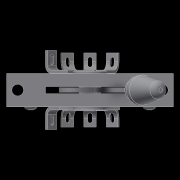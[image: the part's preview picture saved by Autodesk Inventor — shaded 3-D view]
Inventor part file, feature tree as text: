
AUTODESK INVENTOR PART (.ipt)
format: ipt  version: 2020 (Build 240168000, 168)  size: 740,352 bytes
history: native  units: in
note: dims shown in document units (in); Inventor stores cm internally (conversion verified against a paired STEP export)
features: other x22, extrude x20, projected_geometry x5, fillet x3, mirror x1, sketch x1
ambient origin geometry x8: Origin, YZ Plane, XZ Plane, XY Plane, X Axis, Y Axis, Z Axis, Center Point
bodies: Solid3 (feature_tree), Solid5 (feature_tree), Solid6 (feature_tree), Solid7 (feature_tree), Solid8 (feature_tree)
feature tree (52):
  other  "TopProfile"
  extrude  "FrontPanelFeature"  Depth=0.1in
  extrude  "SideFeature"  Depth=0.1in
  other  "SideProfile"
  extrude  "SideProfileFeature"  Depth=0.1in
  extrude  "SideMountsFeature"  Depth=0.1in
  extrude  "MiddleExtrusionFeature"  Depth=0.1in
  extrude  "SideIndentsFeature"  Depth=0.1in
  extrude  "ConnectorsFeature"  Depth=0.1in
  extrude  "MiddleAxisFeature"  Depth=0.1in
  extrude  "DiskFeature"  Depth=0.1in
  extrude  "DiskIndentFeature"  Depth=0.1in TaperAngle=0.0deg
  extrude  "DiskMountsFeature"  Depth=0.1in
  fillet  "DiskMountFilletsFeature"  Radius=0.17in
  other  "MidPlane"
  extrude  "NeckFeature"  Depth=0.1in
  extrude  "HeadFeature"  Depth=0.1in
  extrude  "HeadTopFeature"  Depth=0.1in
  fillet  "HeadFilletFeature"  Radius=0.05in
  fillet  "HeadFillet2Feature"  Radius=0.38in
  other  "OutsideTerminals"
  extrude  "Terminal1Feature"  Depth=0.1in
  extrude  "Terminal2Feature"  Depth=0.1in
  extrude  "Terminal3Feature"  Depth=0.1in
  extrude  "Terminal4Feature"  Depth=0.1in
  extrude  "TerminalLinkFeature"  Depth=0.1in
  extrude  "TerminalEndsFeature"  Depth=0.1in
  other  "TerminalBends"
  other  "TerminalBend1Feature"
  other  "TerminalBend2Feature"
  other  "TerminalBend3Feature"
  other  "TerminalBend4Feature"
  mirror  "TerminalsMirrorFeature"
  other  "TerminalsCombineFeature"
  other  "Side"
  projected_geometry  "Projected Loop5"
  other  "Connectors"
  other  "MiddleAxis"
  projected_geometry  "Projected Loop6"
  other  "Disk"
  other  "DiskIndent"
  projected_geometry  "Projected Loop7"
  other  "DiskMounts"
  other  "Neck"
  other  "Head"
  projected_geometry  "Projected Loop8"
  other  "HeadTop"
  projected_geometry  "Projected Loop9"
  other  "TerminalLink"
  other  "TerminalEnds"
  sketch  "Sketch38"  dims[d129=0.0325in d130=0.0in d146=0.375in d147=1.875in d175=0.1325in d176=1.0in d177=0.08in d178=0.125in d179=0.125in d180=1.625in d181=0.0325in d182=1.2225in d183=0.0in d184=0.1665in d186=0.17in d188=0.1in d190=0.613in d191=0.25in d192=0.05in d193=0.38in d196=0.725in d197=0.015in d198=0.015in d199=0.055in d200=0.055in d201=0.055in d202=0.055in d203=0.055in d204=0.055in d205=0.055in d206=0.0in d207=0.0in d208=0.05in d209=0.0in d210=0.025in d211=0.0in d212=0.02in d213=0.0in d214=0.155in d215=0.1in d216=0.02in d217=0.0in d218=0.25in d219=0.02in d220=0.0in d221=0.035in d222=0.0in d223=0.025in d224=0.035in d225=0.0in d226=0.035in d227=0.0in d228=0.05in d229=0.7in d230=60.0deg d231=1.5in d232=1.0in d233=0.25in d234=0.05in d235=0.0in d236=0.14in d237=0.1443in d238=0.3575in d239=0.45in d240=-0.0756in d241=0.08in d242=0.15in d243=0.1512in d244=0.1512in d245=0.1512in d246=0.14in d247=0.2952in d248=0.2952in d249=0.2952in d250=0.2in d251=0.05in d252=0.07in d253=0.07in d254=0.035in d255=0.0in d256=0.2952in d257=0.07in d258=0.07in d259=0.07in d260=0.07in d261=0.07in d262=0.07in d263=1.0in d264=0.0in d265=1.0in d266=0.0in d267=1.0in d268=0.0in d269=0.1374in d270=0.1718in d271=1.0in d272=0.0in d273=0.01in d274=0.0in d275=0.25in d276=0.25in d277=0.25in d278=0.25in d279=0.05in d280=90.0deg d281=0.1in d282=90.0deg d283=0.1in d284=90.0deg d285=0.1in d286=90.0deg]
  other  "TerminalBend4"
